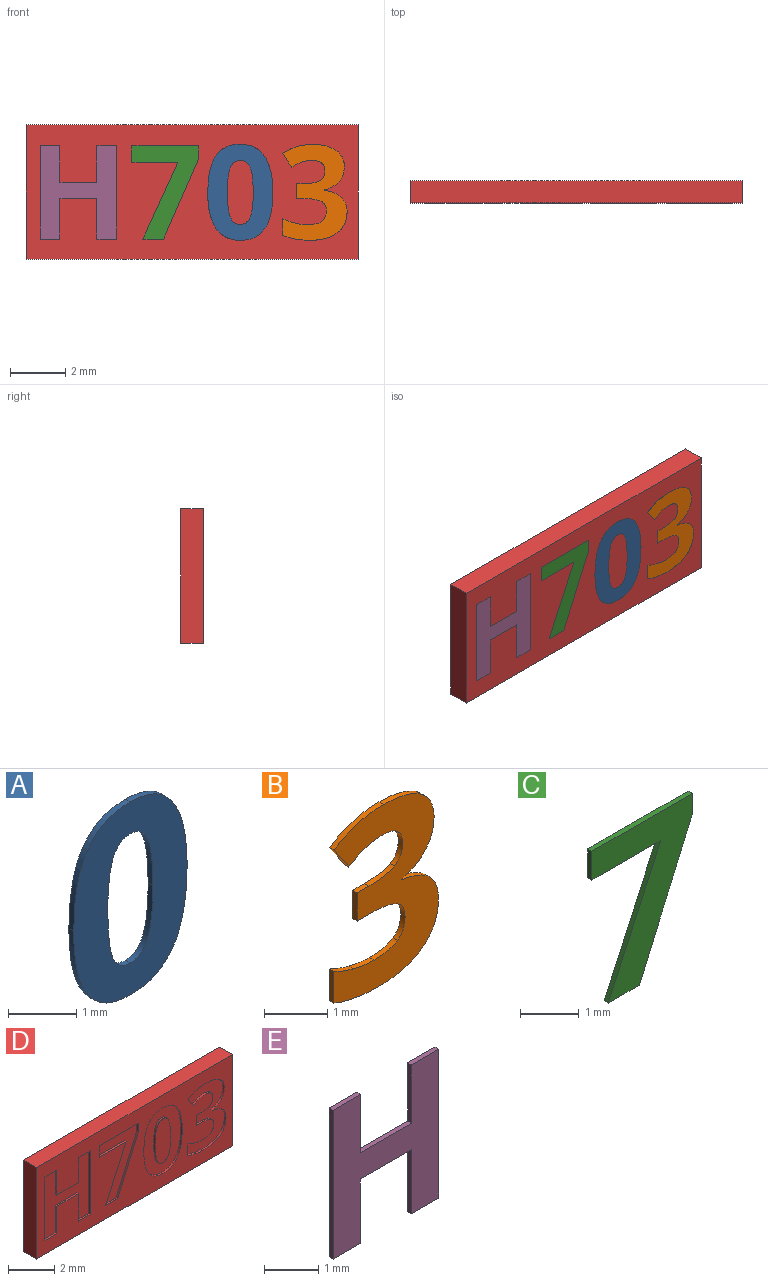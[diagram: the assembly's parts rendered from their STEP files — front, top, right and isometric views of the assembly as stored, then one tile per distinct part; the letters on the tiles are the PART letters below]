
ASSEMBLY  parts=5 mates=4
PART A: 18 faces, bbox 2.4x0.1x3.5 mm
  f0: plane 3.47x2.36mm, normal (0,-1,0), area 5mm2, adj f1,f2,f3,f4,f5,f6,f7,f8
  f1: extruded ~0.88x0.44mm, area 0.1mm2, adj f0,f2,f11,f13
  f2: extruded ~0.89x0.42mm, area 0.1mm2, adj f0,f1,f3,f11
  f3: extruded ~1.32x0.29mm, area 0.1mm2, adj f0,f2,f4,f11
  f4: extruded ~1.29x0.3mm, area 0.1mm2, adj f0,f3,f5,f11
  f5: extruded ~0.88x0.44mm, area 0.1mm2, adj f0,f4,f11,f12
  f6: extruded ~0.36x0.27mm, area 0mm2, adj f0,f7,f11,f16
  f7: extruded ~0.36x0.27mm, area 0mm2, adj f0,f6,f8,f11
  f8: extruded ~0.89x0.11mm, area 0.1mm2, adj f0,f7,f9,f11
  f9: extruded ~0.89x0.11mm, area 0.1mm2, adj f0,f8,f10,f11
  f10: extruded ~0.36x0.27mm, area 0mm2, adj f0,f9,f11,f15
  f11: plane 3.47x2.36mm, normal (0,1,0), area 5mm2, adj f1,f2,f3,f4,f5,f6,f7,f8
  f12: extruded ~0.89x0.42mm, area 0.1mm2, adj f0,f5,f11,f14
  f13: extruded ~1.3x0.3mm, area 0.1mm2, adj f0,f1,f11,f14
  f14: extruded ~1.31x0.29mm, area 0.1mm2, adj f0,f11,f12,f13
  f15: extruded ~0.36x0.27mm, area 0mm2, adj f0,f10,f11,f17
  f16: extruded ~0.89x0.11mm, area 0.1mm2, adj f0,f6,f11,f17
  f17: extruded ~0.89x0.11mm, area 0.1mm2, adj f0,f11,f15,f16
PART B: 29 faces, bbox 2.3x0.1x3.5 mm
  f0: plane 3.47x2.33mm, normal (0,-1,0), area 4.3mm2, adj f1,f2,f3,f4,f5,f6,f7,f8
  f1: extruded ~0.83x0.21mm, area 0.1mm2, adj f0,f2,f25,f27
  f2: extruded ~1.1x0.33mm, area 0.1mm2, adj f0,f1,f3,f25
  f3: plane 0.49x0.33mm, normal (-0.83,0,-0.56), area 0.1mm2, adj f0,f2,f4,f25
  f4: extruded ~0.38x0.19mm, area 0mm2, adj f0,f3,f5,f25
  f5: extruded ~0.34x0.1mm, area 0mm2, adj f0,f4,f6,f25
  f6: extruded ~0.48x0.38mm, area 0.1mm2, adj f0,f5,f7,f25
  f7: extruded ~0.35x0.18mm, area 0mm2, adj f0,f6,f8,f25
  f8: extruded ~0.57x0.1mm, area 0.1mm2, adj f0,f7,f9,f25
  f9: plane 0.26x0.1mm, normal (0,0,1), area 0mm2, adj f0,f8,f10,f25
  f10: plane 0.55x0.1mm, normal (-1,0,0), area 0.1mm2, adj f0,f9,f11,f25
  f11: plane 0.26x0.1mm, normal (0,0,-1), area 0mm2, adj f0,f10,f12,f25
  f12: extruded ~0.62x0.1mm, area 0.1mm2, adj f0,f11,f13,f25
  f13: extruded ~0.34x0.19mm, area 0mm2, adj f0,f12,f14,f25
  f14: extruded ~0.39x0.17mm, area 0mm2, adj f0,f13,f15,f25
  f15: extruded ~0.52x0.12mm, area 0.1mm2, adj f0,f14,f16,f25
  f16: extruded ~0.47x0.1mm, area 0mm2, adj f0,f15,f17,f25
  f17: extruded ~0.43x0.16mm, area 0mm2, adj f0,f16,f18,f25
  f18: plane 0.61x0.1mm, normal (-1,0,0), area 0.1mm2, adj f0,f17,f19,f25
  f19: extruded ~0.97x0.18mm, area 0.1mm2, adj f0,f18,f20,f25
  f20: extruded ~1.01x0.27mm, area 0.1mm2, adj f0,f19,f21,f25
  f21: extruded ~0.76x0.35mm, area 0.1mm2, adj f0,f20,f22,f25
  f22: extruded ~0.53x0.21mm, area 0.1mm2, adj f0,f21,f23,f25
  f23: extruded ~0.62x0.25mm, area 0.1mm2, adj f0,f22,f24,f25
  f24: plane 0.1x0.01mm, normal (1,0,0), area 0mm2, adj f0,f23,f25,f26
  f25: plane 3.47x2.33mm, normal (0,1,0), area 4.3mm2, adj f1,f2,f3,f4,f5,f6,f7,f8
  f26: extruded ~0.54x0.3mm, area 0.1mm2, adj f0,f24,f25,f28
  f27: extruded ~0.59x0.3mm, area 0.1mm2, adj f0,f1,f25,f28
  f28: extruded ~0.54x0.19mm, area 0.1mm2, adj f0,f25,f26,f27
PART C: 9 faces, bbox 2.4x0.1x3.4 mm
  f0: plane 3.37x2.42mm, normal (0,-1,0), area 3.4mm2, adj f1,f2,f3,f4,f6,f7,f8
  f1: plane 2.92x1.28mm, normal (0.92,0,-0.4), area 0.3mm2, adj f0,f2,f5,f7
  f2: plane 0.45x0.1mm, normal (1,0,0), area 0mm2, adj f0,f1,f3,f5
  f3: plane 2.42x0.1mm, normal (0,0,1), area 0.2mm2, adj f0,f2,f4,f5
  f4: plane 0.6x0.1mm, normal (-1,0,0), area 0.1mm2, adj f0,f3,f5,f6
  f5: plane 3.37x2.42mm, normal (0,1,0), area 3.4mm2, adj f1,f2,f3,f4,f6,f7,f8
  f6: plane 1.66x0.1mm, normal (0,0,-1), area 0.2mm2, adj f0,f4,f5,f8
  f7: plane 0.75x0.1mm, normal (0,0,-1), area 0.1mm2, adj f0,f1,f5,f8
  f8: plane 2.77x1.27mm, normal (-0.91,0,0.42), area 0.3mm2, adj f0,f5,f6,f7
PART D: 73 faces, bbox 12x0.8x4.9 mm
  f0: plane 12x4.85mm, normal (0,-1,0), area 38mm2, adj f1,f2,f3,f4,f6,f7,f8,f9
  f1: plane 12x0.8mm, normal (0,0,-1), area 9.6mm2, adj f0,f2,f4,f5
  f2: plane 4.85x0.8mm, normal (1,0,0), area 3.9mm2, adj f0,f1,f3,f5
  f3: plane 12x0.8mm, normal (0,0,1), area 9.6mm2, adj f0,f2,f4,f5
  f4: plane 4.85x0.8mm, normal (-1,0,0), area 3.9mm2, adj f0,f1,f3,f5
  f5: plane 12x4.85mm, normal (0,1,0), area 58.2mm2, adj f1,f2,f3,f4
  f6: plane 0.75x0.1mm, normal (0,0,1), area 0.1mm2, adj f0,f7,f12,f13
  f7: plane 2.92x1.28mm, normal (-0.92,0,0.4), area 0.3mm2, adj f0,f6,f8,f13
  f8: plane 0.45x0.1mm, normal (-1,0,0), area 0mm2, adj f0,f7,f9,f13
  f9: plane 2.42x0.1mm, normal (0,0,-1), area 0.2mm2, adj f0,f8,f10,f13
  f10: plane 0.6x0.1mm, normal (1,0,0), area 0.1mm2, adj f0,f9,f11,f13
  f11: plane 1.66x0.1mm, normal (0,0,1), area 0.2mm2, adj f0,f10,f12,f13
  f12: plane 2.77x1.27mm, normal (0.91,0,-0.42), area 0.3mm2, adj f0,f6,f11,f13
  f13: plane 3.37x2.42mm, normal (0,-1,0), area 3.4mm2, adj f6,f7,f8,f9,f10,f11,f12
  f14: extruded ~0.59x0.3mm, area 0.1mm2, adj f0,f15,f40,f41
  f15: extruded ~0.83x0.21mm, area 0.1mm2, adj f0,f14,f16,f41
  f16: extruded ~1.1x0.33mm, area 0.1mm2, adj f0,f15,f17,f41
  f17: plane 0.49x0.33mm, normal (0.83,0,0.56), area 0.1mm2, adj f0,f16,f18,f41
  f18: extruded ~0.38x0.19mm, area 0mm2, adj f0,f17,f19,f41
  f19: extruded ~0.34x0.1mm, area 0mm2, adj f0,f18,f20,f41
  f20: extruded ~0.48x0.38mm, area 0.1mm2, adj f0,f19,f21,f41
  f21: extruded ~0.35x0.18mm, area 0mm2, adj f0,f20,f22,f41
  f22: extruded ~0.57x0.1mm, area 0.1mm2, adj f0,f21,f23,f41
  f23: plane 0.26x0.1mm, normal (0,0,-1), area 0mm2, adj f0,f22,f24,f41
  f24: plane 0.55x0.1mm, normal (1,0,0), area 0.1mm2, adj f0,f23,f25,f41
  f25: plane 0.26x0.1mm, normal (0,0,1), area 0mm2, adj f0,f24,f26,f41
  f26: extruded ~0.62x0.1mm, area 0.1mm2, adj f0,f25,f27,f41
  f27: extruded ~0.34x0.19mm, area 0mm2, adj f0,f26,f28,f41
  f28: extruded ~0.39x0.17mm, area 0mm2, adj f0,f27,f29,f41
  f29: extruded ~0.52x0.12mm, area 0.1mm2, adj f0,f28,f30,f41
  f30: extruded ~0.47x0.1mm, area 0mm2, adj f0,f29,f31,f41
  f31: extruded ~0.43x0.16mm, area 0mm2, adj f0,f30,f32,f41
  f32: plane 0.61x0.1mm, normal (1,0,0), area 0.1mm2, adj f0,f31,f33,f41
  f33: extruded ~0.97x0.18mm, area 0.1mm2, adj f0,f32,f34,f41
  f34: extruded ~1.01x0.27mm, area 0.1mm2, adj f0,f33,f35,f41
  f35: extruded ~0.76x0.35mm, area 0.1mm2, adj f0,f34,f36,f41
  f36: extruded ~0.53x0.21mm, area 0.1mm2, adj f0,f35,f37,f41
  f37: extruded ~0.62x0.25mm, area 0.1mm2, adj f0,f36,f38,f41
  f38: plane 0.1x0.01mm, normal (-1,0,0), area 0mm2, adj f0,f37,f39,f41
  f39: extruded ~0.54x0.3mm, area 0.1mm2, adj f0,f38,f40,f41
  f40: extruded ~0.54x0.19mm, area 0.1mm2, adj f0,f14,f39,f41
  f41: plane 3.47x2.33mm, normal (0,-1,0), area 4.3mm2, adj f14,f15,f16,f17,f18,f19,f20,f21
  f42: extruded ~1.3x0.3mm, area 0.1mm2, adj f0,f43,f57,f58
  f43: extruded ~0.88x0.44mm, area 0.1mm2, adj f0,f42,f44,f58
  f44: extruded ~0.89x0.42mm, area 0.1mm2, adj f0,f43,f45,f58
  f45: extruded ~1.32x0.29mm, area 0.1mm2, adj f0,f44,f46,f58
  f46: extruded ~1.29x0.3mm, area 0.1mm2, adj f0,f45,f47,f58
  f47: extruded ~0.88x0.44mm, area 0.1mm2, adj f0,f46,f48,f58
  f48: extruded ~0.89x0.42mm, area 0.1mm2, adj f0,f47,f57,f58
  f49: extruded ~0.89x0.11mm, area 0.1mm2, adj f50,f56,f58,f59
  f50: extruded ~0.36x0.27mm, area 0mm2, adj f49,f51,f58,f59
  f51: extruded ~0.36x0.27mm, area 0mm2, adj f50,f52,f58,f59
  f52: extruded ~0.89x0.11mm, area 0.1mm2, adj f51,f53,f58,f59
  f53: extruded ~0.89x0.11mm, area 0.1mm2, adj f52,f54,f58,f59
  f54: extruded ~0.36x0.27mm, area 0mm2, adj f53,f55,f58,f59
  f55: extruded ~0.36x0.27mm, area 0mm2, adj f54,f56,f58,f59
  f56: extruded ~0.89x0.11mm, area 0.1mm2, adj f49,f55,f58,f59
  f57: extruded ~1.31x0.29mm, area 0.1mm2, adj f0,f42,f48,f58
  f58: plane 3.47x2.36mm, normal (0,-1,0), area 5mm2, adj f42,f43,f44,f45,f46,f47,f48,f49
  f59: plane 2.32x0.94mm, normal (0,-1,0), area 1.8mm2, adj f49,f50,f51,f52,f53,f54,f55,f56
  f60: plane 3.37x0.1mm, normal (-1,0,0), area 0.3mm2, adj f0,f61,f71,f72
  f61: plane 0.71x0.1mm, normal (0,0,-1), area 0.1mm2, adj f0,f60,f62,f72
  f62: plane 1.32x0.1mm, normal (1,0,0), area 0.1mm2, adj f0,f61,f63,f72
  f63: plane 1.33x0.1mm, normal (0,0,-1), area 0.1mm2, adj f0,f62,f64,f72
  f64: plane 1.32x0.1mm, normal (-1,0,0), area 0.1mm2, adj f0,f63,f65,f72
  f65: plane 0.72x0.1mm, normal (0,0,-1), area 0.1mm2, adj f0,f64,f66,f72
  f66: plane 3.37x0.1mm, normal (1,0,0), area 0.3mm2, adj f0,f65,f67,f72
  f67: plane 0.72x0.1mm, normal (0,0,1), area 0.1mm2, adj f0,f66,f68,f72
  f68: plane 1.46x0.1mm, normal (-1,0,0), area 0.1mm2, adj f0,f67,f69,f72
  f69: plane 1.33x0.1mm, normal (0,0,1), area 0.1mm2, adj f0,f68,f70,f72
  f70: plane 1.46x0.1mm, normal (1,0,0), area 0.1mm2, adj f0,f69,f71,f72
  f71: plane 0.71x0.1mm, normal (0,0,1), area 0.1mm2, adj f0,f60,f70,f72
  f72: plane 3.37x2.76mm, normal (0,-1,0), area 5.6mm2, adj f60,f61,f62,f63,f64,f65,f66,f67
PART E: 14 faces, bbox 2.8x0.1x3.4 mm
  f0: plane 3.37x2.76mm, normal (0,-1,0), area 5.6mm2, adj f1,f2,f3,f4,f5,f6,f7,f8
  f1: plane 0.71x0.1mm, normal (0,0,1), area 0.1mm2, adj f0,f2,f10,f12
  f2: plane 1.32x0.1mm, normal (-1,0,0), area 0.1mm2, adj f0,f1,f3,f10
  f3: plane 1.33x0.1mm, normal (0,0,1), area 0.1mm2, adj f0,f2,f4,f10
  f4: plane 1.32x0.1mm, normal (1,0,0), area 0.1mm2, adj f0,f3,f5,f10
  f5: plane 0.72x0.1mm, normal (0,0,1), area 0.1mm2, adj f0,f4,f6,f10
  f6: plane 3.37x0.1mm, normal (-1,0,0), area 0.3mm2, adj f0,f5,f7,f10
  f7: plane 0.72x0.1mm, normal (0,0,-1), area 0.1mm2, adj f0,f6,f8,f10
  f8: plane 1.46x0.1mm, normal (1,0,0), area 0.1mm2, adj f0,f7,f9,f10
  f9: plane 1.33x0.1mm, normal (0,0,-1), area 0.1mm2, adj f0,f8,f10,f11
  f10: plane 3.37x2.76mm, normal (0,1,0), area 5.6mm2, adj f1,f2,f3,f4,f5,f6,f7,f8
  f11: plane 1.46x0.1mm, normal (-1,0,0), area 0.1mm2, adj f0,f9,f10,f13
  f12: plane 3.37x0.1mm, normal (1,0,0), area 0.3mm2, adj f0,f1,f10,f13
  f13: plane 0.71x0.1mm, normal (0,0,-1), area 0.1mm2, adj f0,f10,f11,f12
PLACE A t=(-1.12,0.37,-0.03)mm
PLACE B t=(2.91,0.37,-0.03)mm
PLACE C t=(-2.46,0.37,-0.03)mm
PLACE D t=(-0.02,0.37,-0.03)mm
PLACE E t=(-0.02,0.37,-0.03)mm
MATE fastened C.f0 <-> D.f0  axis (0,-1,0) through (-1.8,-0.43,-1.73)mm
MATE fastened E.f0 <-> D.f0  axis (0,-1,0) through (-5.51,-0.43,-1.73)mm
MATE fastened A.f0 <-> D.f59  axis (0,-1,0) through (1.72,-0.43,-1.2)mm
MATE fastened B.f0 <-> D.f0  axis (0,-1,0) through (3.25,-0.43,-1.59)mm
